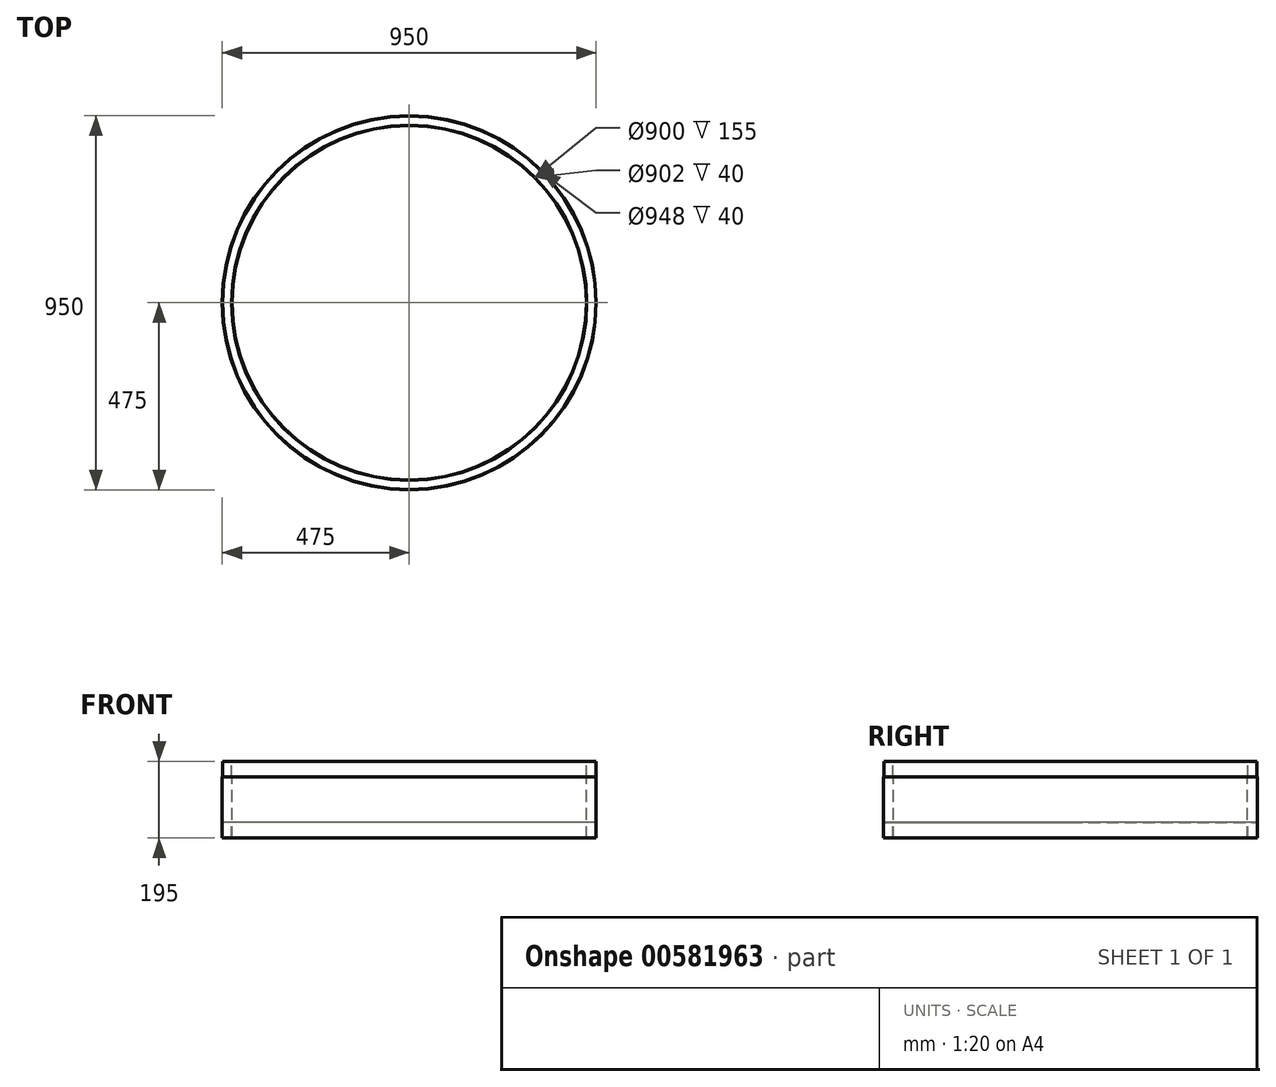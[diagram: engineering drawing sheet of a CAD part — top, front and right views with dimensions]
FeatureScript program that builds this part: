
annotation { "Feature Type Name" : "Feature", "Feature Type Description" : "" }
export const myFeature = defineFeature(function(context is Context, id is Id, definition is map)
    precondition{}
    {
        {
            var Q0;
            Q0=qCreatedBy(makeId("Front.planeOp"),FACE);
            var sketch = newSketch(context, id + "F0", { "sketchPlane" : qUnion([Q0])});
            skLineSegment(sketch, "E0", {"start": v(0, 345.75) * mm, "end": v(0, -558.03) * mm, "construction": true});
            skLineSegment(sketch, "E1", {"start": v(-450, -518.84) * mm, "end": v(-450, -363.84) * mm});
            skLineSegment(sketch, "E2", {"start": v(-450, -363.84) * mm, "end": v(-451, -363.84) * mm});
            skLineSegment(sketch, "E3", {"start": v(-451, -363.84) * mm, "end": v(-451, -323.84) * mm});
            skLineSegment(sketch, "E4", {"start": v(-451, -323.84) * mm, "end": v(-474, -323.84) * mm});
            skLineSegment(sketch, "E5", {"start": v(-474, -323.84) * mm, "end": v(-474, -363.84) * mm});
            skLineSegment(sketch, "E6", {"start": v(-474, -363.84) * mm, "end": v(-475, -363.84) * mm});
            skLineSegment(sketch, "E7", {"start": v(-475, -363.84) * mm, "end": v(-475, -518.84) * mm});
            skLineSegment(sketch, "E8", {"start": v(-475, -518.84) * mm, "end": v(-474, -518.84) * mm});
            skLineSegment(sketch, "E9", {"start": v(-474, -518.84) * mm, "end": v(-474, -478.84) * mm});
            skLineSegment(sketch, "E10", {"start": v(-474, -478.84) * mm, "end": v(-451, -478.84) * mm});
            skLineSegment(sketch, "E11", {"start": v(-451, -478.84) * mm, "end": v(-451, -518.84) * mm});
            skLineSegment(sketch, "E12", {"start": v(-451, -518.84) * mm, "end": v(-450, -518.84) * mm});
            skSolve(sketch);
        }
        {
            var Q0;
            Q0=qSketchRegion(id+"F0",true);
            var Q1;
            Q1=sQuery(id+"F0.wireOp",EDGE,"E0");
            revolve(context, id + "F1", {"entities" : qUnion([Q0]), "axis" : qUnion([Q1]), "revolveType" : RevolveType.FULL});
        }
    });
